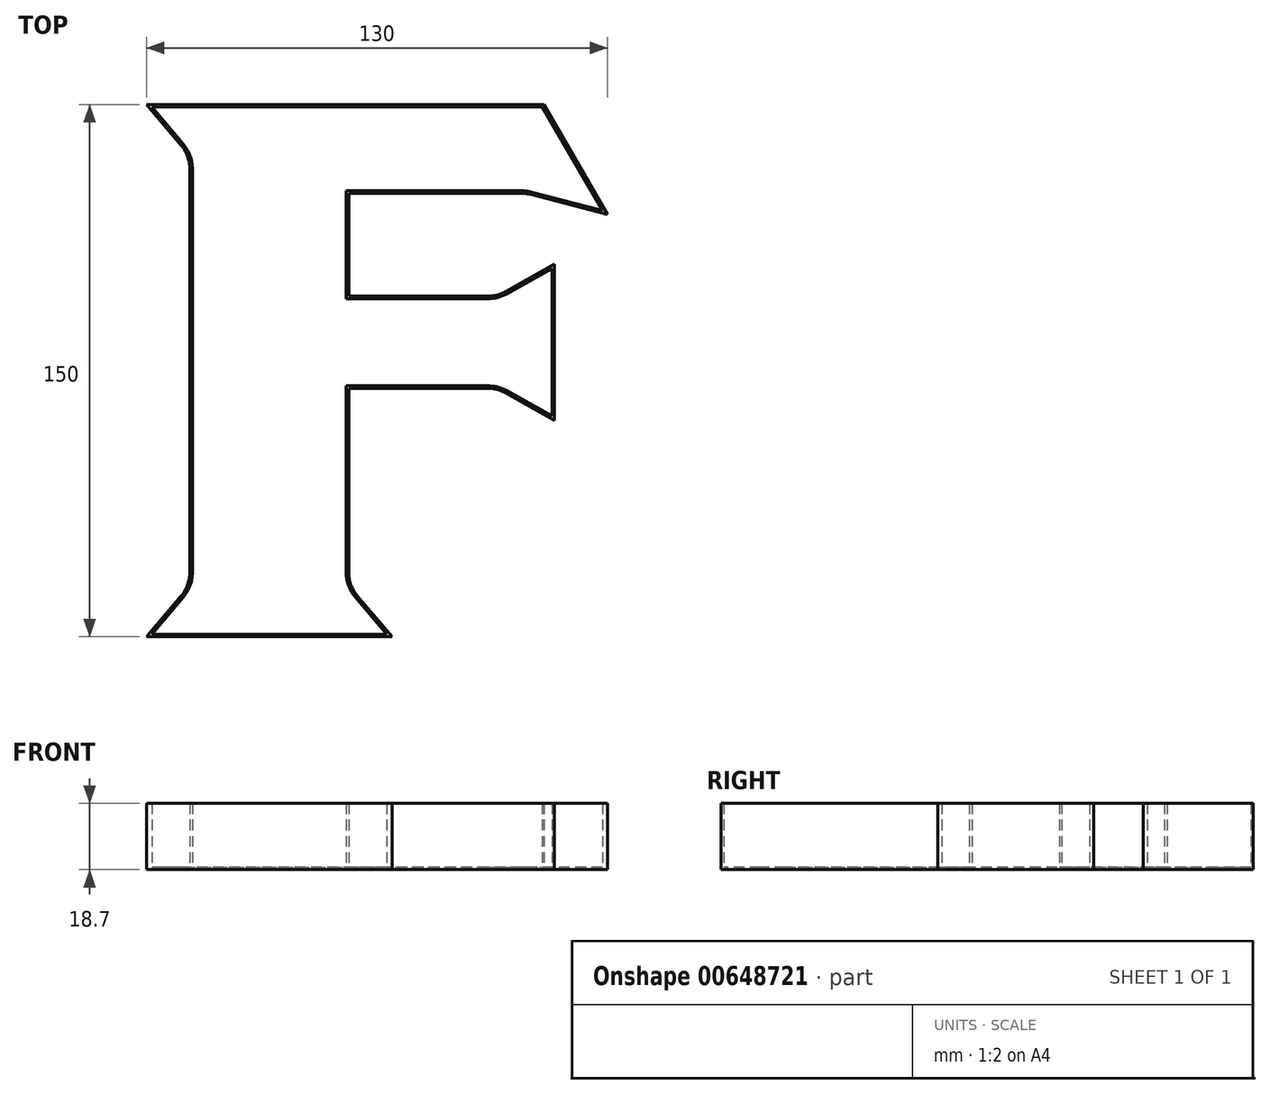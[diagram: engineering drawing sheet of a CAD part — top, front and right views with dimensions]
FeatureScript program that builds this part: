
annotation { "Feature Type Name" : "Feature", "Feature Type Description" : "" }
export const myFeature = defineFeature(function(context is Context, id is Id, definition is map)
    precondition{}
    {
        {
            var Q0;
            Q0=qCreatedBy(makeId("Top.planeOp"),FACE);
            var sketch = newSketch(context, id + "F0", { "sketchPlane" : qUnion([Q0])});
            skLineSegment(sketch, "E0", {"start": v(-55.12, 63.38) * mm, "end": v(-65, 75) * mm});
            skLineSegment(sketch, "E1", {"start": v(-65, 75) * mm, "end": v(47, 75) * mm});
            skLineSegment(sketch, "E2", {"start": v(47, 75) * mm, "end": v(65, 44) * mm});
            skLineSegment(sketch, "E3", {"start": v(65, 44) * mm, "end": v(43.24, 49.68) * mm});
            skArc(sketch, "E4", {"start": v(43.24, 49.68) * mm, "mid": v(42, 49.92) * mm, "end": v(40.72, 50) * mm});
            skLineSegment(sketch, "E5", {"start": v(40.72, 50) * mm, "end": v(-8, 50) * mm});
            skLineSegment(sketch, "E6", {"start": v(-8, 50) * mm, "end": v(-8, 21) * mm});
            skLineSegment(sketch, "E7", {"start": v(-8, 21) * mm, "end": v(31.38, 21) * mm});
            skArc(sketch, "E8", {"start": v(31.38, 21) * mm, "mid": v(33.92, 21.33) * mm, "end": v(36.29, 22.28) * mm});
            skLineSegment(sketch, "E9", {"start": v(36.29, 22.28) * mm, "end": v(50, 30) * mm});
            skLineSegment(sketch, "E10", {"start": v(50, 30) * mm, "end": v(50, -14) * mm});
            skLineSegment(sketch, "E11", {"start": v(50, -14) * mm, "end": v(36.29, -6.28) * mm});
            skArc(sketch, "E12", {"start": v(36.29, -6.28) * mm, "mid": v(33.92, -5.33) * mm, "end": v(31.38, -5) * mm});
            skLineSegment(sketch, "E13", {"start": v(31.38, -5) * mm, "end": v(-8, -5) * mm});
            skLineSegment(sketch, "E14", {"start": v(-8, -5) * mm, "end": v(-8, -56.9) * mm});
            skArc(sketch, "E15", {"start": v(-8, -56.9) * mm, "mid": v(-7.38, -60.36) * mm, "end": v(-5.62, -63.38) * mm});
            skLineSegment(sketch, "E16", {"start": v(-5.62, -63.38) * mm, "end": v(4.26, -75) * mm});
            skLineSegment(sketch, "E17", {"start": v(4.26, -75) * mm, "end": v(-65, -75) * mm});
            skLineSegment(sketch, "E18", {"start": v(-65, -75) * mm, "end": v(-55.12, -63.38) * mm});
            skArc(sketch, "E19", {"start": v(-55.12, -63.38) * mm, "mid": v(-53.36, -60.36) * mm, "end": v(-52.74, -56.9) * mm});
            skLineSegment(sketch, "E20", {"start": v(-52.74, -56.9) * mm, "end": v(-52.74, 56.9) * mm});
            skArc(sketch, "E21", {"start": v(-52.74, 56.9) * mm, "mid": v(-53.36, 60.35) * mm, "end": v(-55.12, 63.38) * mm});
            skLineSegment(sketch, "E22", {"start": v(-54.6, 63.83) * mm, "end": v(-63.49, 74.3) * mm});
            skLineSegment(sketch, "E23", {"start": v(-63.49, 74.3) * mm, "end": v(46.6, 74.3) * mm});
            skLineSegment(sketch, "E24", {"start": v(46.6, 74.3) * mm, "end": v(63.55, 45.1) * mm});
            skLineSegment(sketch, "E25", {"start": v(63.55, 45.1) * mm, "end": v(43.42, 50.35) * mm});
            skArc(sketch, "E26", {"start": v(43.42, 50.35) * mm, "mid": v(42.08, 50.61) * mm, "end": v(40.72, 50.7) * mm});
            skLineSegment(sketch, "E27", {"start": v(40.72, 50.7) * mm, "end": v(-8.7, 50.7) * mm});
            skLineSegment(sketch, "E28", {"start": v(-8.7, 50.7) * mm, "end": v(-8.7, 20.3) * mm});
            skLineSegment(sketch, "E29", {"start": v(-8.7, 20.3) * mm, "end": v(31.38, 20.3) * mm});
            skArc(sketch, "E30", {"start": v(31.38, 20.3) * mm, "mid": v(34.1, 20.65) * mm, "end": v(36.63, 21.67) * mm});
            skLineSegment(sketch, "E31", {"start": v(36.63, 21.67) * mm, "end": v(49.3, 28.8) * mm});
            skLineSegment(sketch, "E32", {"start": v(49.3, 28.8) * mm, "end": v(49.3, -12.8) * mm});
            skLineSegment(sketch, "E33", {"start": v(49.3, -12.8) * mm, "end": v(36.63, -5.67) * mm});
            skArc(sketch, "E34", {"start": v(36.63, -5.67) * mm, "mid": v(34.1, -4.65) * mm, "end": v(31.38, -4.3) * mm});
            skLineSegment(sketch, "E35", {"start": v(31.38, -4.3) * mm, "end": v(-8.7, -4.3) * mm});
            skLineSegment(sketch, "E36", {"start": v(-8.7, -4.3) * mm, "end": v(-8.7, -56.9) * mm});
            skArc(sketch, "E37", {"start": v(-8.7, -56.9) * mm, "mid": v(-8.04, -60.6) * mm, "end": v(-6.15, -63.84) * mm});
            skLineSegment(sketch, "E38", {"start": v(-6.15, -63.84) * mm, "end": v(2.74, -74.3) * mm});
            skLineSegment(sketch, "E39", {"start": v(2.74, -74.3) * mm, "end": v(-63.48, -74.3) * mm});
            skLineSegment(sketch, "E40", {"start": v(-63.48, -74.3) * mm, "end": v(-54.6, -63.84) * mm});
            skArc(sketch, "E41", {"start": v(-54.6, -63.84) * mm, "mid": v(-52.7, -60.6) * mm, "end": v(-52.04, -56.9) * mm});
            skLineSegment(sketch, "E42", {"start": v(-52.04, -56.9) * mm, "end": v(-52.04, 56.9) * mm});
            skArc(sketch, "E43", {"start": v(-52.04, 56.9) * mm, "mid": v(-52.7, 60.6) * mm, "end": v(-54.6, 63.83) * mm});
            skSolve(sketch);
        }
        {
            var Q0;
            Q0=makeQuery(id+"F0.imprint","IMPRINT",FACE,{"disambiguationData":[TD([[makeQuery(id+"F0.imprint","IMPRINT",EDGE,{"derivedFrom":sQuery(id+"F0.wireOp",EDGE,"bbe9bcc9-d039-4052-9a4d-74e69b2f70c6")}),-1.0]])]});
            var Q1;
            Q1=makeQuery(id+"F0.imprint","IMPRINT",FACE,{"disambiguationData":[TD([[makeQuery(id+"F0.imprint","IMPRINT",EDGE,{"derivedFrom":sQuery(id+"F0.wireOp",EDGE,"144fdc90-ca91-478e-9ea8-37da4d5221f9")}),-1.0]])]});
            var Q2;
            Q2=makeQuery(id+"F0.imprint","IMPRINT",FACE,{"disambiguationData":[TD([[makeQuery(id+"F0.imprint","IMPRINT",EDGE,{"derivedFrom":sQuery(id+"F0.wireOp",EDGE,"E0")}),-1.0]])]});
            var Q3;
            Q3=makeQuery(id+"F0.imprint","IMPRINT",FACE,{"disambiguationData":[TD([[makeQuery(id+"F0.imprint","IMPRINT",EDGE,{"derivedFrom":sQuery(id+"F0.wireOp",EDGE,"E22")}),-1.0]])]});
            var Q4;
            Q4=makeQuery(id+"F0.imprint","IMPRINT",FACE,{"disambiguationData":[TD([[makeQuery(id+"F0.imprint","IMPRINT",EDGE,{"derivedFrom":sQuery(id+"F0.wireOp",EDGE,"3e0c7481-3dda-4920-a3ee-d98c731c7ed2")}),-1.0]])]});
            extrude(context, id + "F1", {"entities" : qUnion([Q0, Q1, Q2, Q3, Q4]), "depth" : 0.7 * mm, "offsetDistance" : 25 * mm});
        }
        {
            var Q0;
            Q0=makeQuery(id+"F1.opExtrude","CAP_FACE",FACE,{"disambiguationData":[OSD([sQuery(id+"F0.wireOp",EDGE,"E0"),sQuery(id+"F0.wireOp",EDGE,"E1"),sQuery(id+"F0.wireOp",EDGE,"E2"),sQuery(id+"F0.wireOp",EDGE,"E3"),sQuery(id+"F0.wireOp",EDGE,"E4"),sQuery(id+"F0.wireOp",EDGE,"E5"),sQuery(id+"F0.wireOp",EDGE,"E6"),sQuery(id+"F0.wireOp",EDGE,"E7"),sQuery(id+"F0.wireOp",EDGE,"E8"),sQuery(id+"F0.wireOp",EDGE,"E9"),sQuery(id+"F0.wireOp",EDGE,"E10"),sQuery(id+"F0.wireOp",EDGE,"E11"),sQuery(id+"F0.wireOp",EDGE,"E12"),sQuery(id+"F0.wireOp",EDGE,"E13"),sQuery(id+"F0.wireOp",EDGE,"E14"),sQuery(id+"F0.wireOp",EDGE,"E15"),sQuery(id+"F0.wireOp",EDGE,"E16"),sQuery(id+"F0.wireOp",EDGE,"E17"),sQuery(id+"F0.wireOp",EDGE,"E18"),sQuery(id+"F0.wireOp",EDGE,"E19"),sQuery(id+"F0.wireOp",EDGE,"E20"),sQuery(id+"F0.wireOp",EDGE,"E21")])],"isStart":false});
            var sketch = newSketch(context, id + "F2", { "sketchPlane" : qUnion([Q0])});
            skLineSegment(sketch, "E44.0", {"start": v(50, -14) * mm, "end": v(36.29, -6.28) * mm});
            skLineSegment(sketch, "E44.1", {"start": v(-8.7, 50.7) * mm, "end": v(-8.7, 20.3) * mm});
            skLineSegment(sketch, "E44.2", {"start": v(47, 75) * mm, "end": v(65, 44) * mm});
            skLineSegment(sketch, "E44.3", {"start": v(65, 44) * mm, "end": v(43.24, 49.68) * mm});
            skArc(sketch, "E44.4", {"start": v(-54.6, -63.84) * mm, "mid": v(-52.7, -60.6) * mm, "end": v(-52.04, -56.9) * mm});
            skLineSegment(sketch, "E44.5", {"start": v(-6.15, -63.84) * mm, "end": v(2.74, -74.3) * mm});
            skLineSegment(sketch, "E44.6", {"start": v(36.29, 22.28) * mm, "end": v(50, 30) * mm});
            skLineSegment(sketch, "E44.7", {"start": v(-63.48, -74.3) * mm, "end": v(-54.6, -63.84) * mm});
            skLineSegment(sketch, "E44.8", {"start": v(4.26, -75) * mm, "end": v(-65, -75) * mm});
            skLineSegment(sketch, "E44.9", {"start": v(-8.7, 20.3) * mm, "end": v(31.38, 20.3) * mm});
            skLineSegment(sketch, "E44.10", {"start": v(-8, 21) * mm, "end": v(31.38, 21) * mm});
            skLineSegment(sketch, "E44.11", {"start": v(40.72, 50.7) * mm, "end": v(-8.7, 50.7) * mm});
            skLineSegment(sketch, "E44.12", {"start": v(-63.49, 74.3) * mm, "end": v(46.6, 74.3) * mm});
            skArc(sketch, "E44.13", {"start": v(-8.7, -56.9) * mm, "mid": v(-8.04, -60.6) * mm, "end": v(-6.15, -63.84) * mm});
            skLineSegment(sketch, "E44.14", {"start": v(-65, -75) * mm, "end": v(-55.12, -63.38) * mm});
            skLineSegment(sketch, "E44.15", {"start": v(31.38, -5) * mm, "end": v(-8, -5) * mm});
            skLineSegment(sketch, "E44.16", {"start": v(-54.6, 63.83) * mm, "end": v(-63.49, 74.3) * mm});
            skLineSegment(sketch, "E44.17", {"start": v(-8.7, -4.3) * mm, "end": v(-8.7, -56.9) * mm});
            skLineSegment(sketch, "E44.18", {"start": v(36.63, 21.67) * mm, "end": v(49.3, 28.8) * mm});
            skLineSegment(sketch, "E44.19", {"start": v(46.6, 74.3) * mm, "end": v(63.55, 45.1) * mm});
            skLineSegment(sketch, "E44.20", {"start": v(-5.62, -63.38) * mm, "end": v(4.26, -75) * mm});
            skLineSegment(sketch, "E44.21", {"start": v(49.3, -12.8) * mm, "end": v(36.63, -5.67) * mm});
            skLineSegment(sketch, "E44.22", {"start": v(49.3, 28.8) * mm, "end": v(49.3, -12.8) * mm});
            skLineSegment(sketch, "E44.23", {"start": v(-52.74, -56.9) * mm, "end": v(-52.74, 56.9) * mm});
            skLineSegment(sketch, "E44.24", {"start": v(63.55, 45.1) * mm, "end": v(43.42, 50.35) * mm});
            skArc(sketch, "E44.25", {"start": v(-52.74, 56.9) * mm, "mid": v(-53.36, 60.35) * mm, "end": v(-55.12, 63.38) * mm});
            skArc(sketch, "E44.26", {"start": v(-8, -56.9) * mm, "mid": v(-7.38, -60.36) * mm, "end": v(-5.62, -63.38) * mm});
            skLineSegment(sketch, "E44.27", {"start": v(-55.12, 63.38) * mm, "end": v(-65, 75) * mm});
            skLineSegment(sketch, "E44.28", {"start": v(-52.04, -56.9) * mm, "end": v(-52.04, 56.9) * mm});
            skArc(sketch, "E44.29", {"start": v(-55.12, -63.38) * mm, "mid": v(-53.36, -60.36) * mm, "end": v(-52.74, -56.9) * mm});
            skArc(sketch, "E44.30", {"start": v(-52.04, 56.9) * mm, "mid": v(-52.7, 60.6) * mm, "end": v(-54.6, 63.83) * mm});
            skLineSegment(sketch, "E45.0", {"start": v(31.38, -4.3) * mm, "end": v(-8.7, -4.3) * mm});
            skPoint(sketch, "E46.0", {"position": v(34.1, -4.65) * mm});
            skArc(sketch, "E47.0", {"start": v(36.63, -5.67) * mm, "mid": v(34.1, -4.65) * mm, "end": v(31.38, -4.3) * mm});
            skArc(sketch, "E48.0", {"start": v(36.29, -6.28) * mm, "mid": v(33.92, -5.33) * mm, "end": v(31.38, -5) * mm});
            skLineSegment(sketch, "E49.0", {"start": v(50, 30) * mm, "end": v(50, -14) * mm});
            skArc(sketch, "E50.0", {"start": v(31.38, 20.3) * mm, "mid": v(34.1, 20.65) * mm, "end": v(36.63, 21.67) * mm});
            skArc(sketch, "E51.0", {"start": v(31.38, 21) * mm, "mid": v(33.92, 21.33) * mm, "end": v(36.29, 22.28) * mm});
            skLineSegment(sketch, "E52.0", {"start": v(-8, 50) * mm, "end": v(-8, 21) * mm});
            skLineSegment(sketch, "E53.0", {"start": v(-8, -5) * mm, "end": v(-8, -56.9) * mm});
            skLineSegment(sketch, "E54.0", {"start": v(40.72, 50) * mm, "end": v(-8, 50) * mm});
            skArc(sketch, "E55.0", {"start": v(43.24, 49.68) * mm, "mid": v(42, 49.92) * mm, "end": v(40.72, 50) * mm});
            skArc(sketch, "E56.0", {"start": v(43.42, 50.35) * mm, "mid": v(42.08, 50.61) * mm, "end": v(40.72, 50.7) * mm});
            skLineSegment(sketch, "E57.0", {"start": v(-65, 75) * mm, "end": v(47, 75) * mm});
            skLineSegment(sketch, "E58.0", {"start": v(2.74, -74.3) * mm, "end": v(-63.48, -74.3) * mm});
            skSolve(sketch);
        }
        {
            var Q0;
            Q0=makeQuery(id+"F2.imprint","IMPRINT",FACE,{"disambiguationData":[TD([[makeQuery(id+"F2.imprint","IMPRINT",EDGE,{"derivedFrom":sQuery(id+"F2.wireOp",EDGE,"E44.0")}),-1.0]])]});
            extrude(context, id + "F3", {"entities" : qUnion([Q0]), "operationType" : NewBodyOperationType.ADD, "depth" : 18 * mm, "offsetDistance" : 25 * mm});
        }
    });
